# Revit family: Shower-Handshower-KOHLER-Shift_Ellipse-K-10109IN
name_source: partatom
category: Plumbing Fixtures
revit_build: Autodesk Revit 2017 (Build: 20160225_1515(x64)
units: mm (PartAtom-declared; Revit-internal decimal feet)

## family parameters
Cut with Voids When Loaded = No
Host = Face
OmniClass Number = 23.31.17.00
OmniClass Title = Showers
Part Type = Normal
Room Calculation Point = No
Round Connector Dimension = Use Diameter
Shared = No

## types (2) — shared parameters
ADA Compliant = No
Assembly Code = D2010700
CW Connection = No
Cold Water Inlet = Cold Water Inlet
Date Modified = 10/29/2020
Default Elevation = 0"
Description = Multi-function handshower with hose and black handle
Drain Included = No
Flow Rate = 0 GPM
HW Connection = Yes
Height = 9"
Hot Water Inlet = Hot Water Inlet
Length = 15/16"
Manufacturer = KOHLER Co.
Master Format 2014 = 22 42 23
Master Format 2014 Name = Residential Showers
Material = Premium Metal Construction
Panel Thickness = 0"
Pressure = 0.00 psi
Product Documentation Link = http://resources.kohler.com
Product Name = Shift_Ellipse
Product Page URL = https://www.kohler.co.in
Tempered Water Inlet = Tempered Water Inlet
URL = https://www.kohler.co.in
Vent Connection = No
Waste Connection = No
Waste Water Outlet = Waste Water Outlet
WaterSense Certified = No
Width = 1 1/8"

## per-type parameters (varying)
| type | Finish | Model | Type |
| CP-Polished Chrome | Kohler-Metal-CP-Polished_Chrome | K-10109IN-CP | 1 |
| AF-Flange Gold | Kohler-Metal-AF-Flange_Gold | K-10109IN-AF | 2 |

## geometry (parser evidence)
native form markers: Sweep x5
no freeform markers — native parametric forms only
